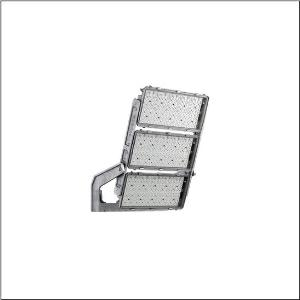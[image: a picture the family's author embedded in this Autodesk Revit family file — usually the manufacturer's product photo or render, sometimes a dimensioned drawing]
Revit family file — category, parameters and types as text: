
# Revit family: floodlight_fl_11_maxi_pro_remote___pl33t_5xa779424t01aa_a9ee
name_source: partatom
category: Lighting Fixtures
units: mm (PartAtom-declared; Revit-internal decimal feet)

## family parameters
Cut with Voids When Loaded = No
Host = Face
Light Source = No
Part Type = Normal
Room Calculation Point = No
Round Connector Dimension = Use Diameter
Shared = No

## types (1)
- --- (1 x LED, 164520 lm, 1539.3 W, 5700K)
    Apparent Load = 1539 VA
    CIE Flux Codes = 27 70 98 100 100
    Color Rendering = 90
    Color Temperature = 5700K
    Default Elevation = 1800 mm
    Description = Floodlight FL 11  maxi  pro Remote floodlight; light control with lens of PMMA; cover panel of toughened safety glass, transparent; light distribution: PL33T, asymmetric direct distribution, LEDcolour temperature: 5700K, rated luminous flux: 164.520lm, colour rendering: CRI > 90, light colour: 957; luminous efficacy: 107lm/W; brightness control: DALI 2 (1 DALI address); with terminal, 8-pole, max. 2.5mm², mains connection: 220..240V/380..400V AC, 50/60Hz, surge voltage resistance: line to ground: 10kV, ECG replaceable separately, no afterglow with DALI off / DMX off command, LED unit replaceable without ESD environment, dustproof LED module, dimming range 10..100%; 1539W floodlight with 3x LED unit of diecast aluminium, coated grey; length: 1.003mm / width: 651mm / height: 338mm; mounting bracket, of diecast aluminium, uncoated, natural, equipment: Power, protection rating (complete): IP66; insulation class (complete): insulation class I (protective earthing); certification: CE, ENEC, VDE; ball protection: ball impact resistant, impact resistance: IK07; only for outdoor installations, rated ambient temperature 10°C, permissible operating ambient temperature: -40..+30°C, permissible storage temperature: -40..+85°C; packaging unit: 1 piece

Light Distribution: PL33T
    Height = 320 mm
    Lamp = 1 x LED
    Lamp Light Flux = 164520 lm
    Lamp Power = 1539.3 W
    Lamp count = 1
    Length = 1002 mm
    Luminous efficacy = 107 lm/W
    Manufacturer = Siteco
    ModVariant = No
    Model = 5XA779424T01AA
    Mounting Place = Ceiling
    Mounting Type = Surface mounted
    Number of Poles = 1
    OnlyDefault = Yes
    Power Factor = 1
    Product Name = Floodlight FL 11 maxi pro Remote | PL33T
    Product group = floodlight | ceiling mounted
    ProductGroupID = 302
    Protection Class = Protection class I
    Protection Degree = IP 66
    RLX_Detail_Level = 1
    RLX_Emergency_Light_Flux = 0 lm
    RLX_Emergency_Type = 0
    RLX_Emergency_Type_DB = No
    RlxData = <blob elided: 52289 chars, md5=fab14a43>
    Socket = socket
    Standby Power = 0 W
    System Light Flux = 164520 lm
    System Power = 1539 W
    Type Comments = factory setting: luminous flux: 100 % | dim-lin: 254 | 1080 mA
    Type Image = l_1006784.jpg
    URL = http://relux.com
    VarID = @adj_011289
    Voltage = 0 V
    Weight = 0.00 kg
    Width = 655 mm

## geometry (parser evidence)
native form markers: Blend x4, Sweep x14
no freeform markers — native parametric forms only
